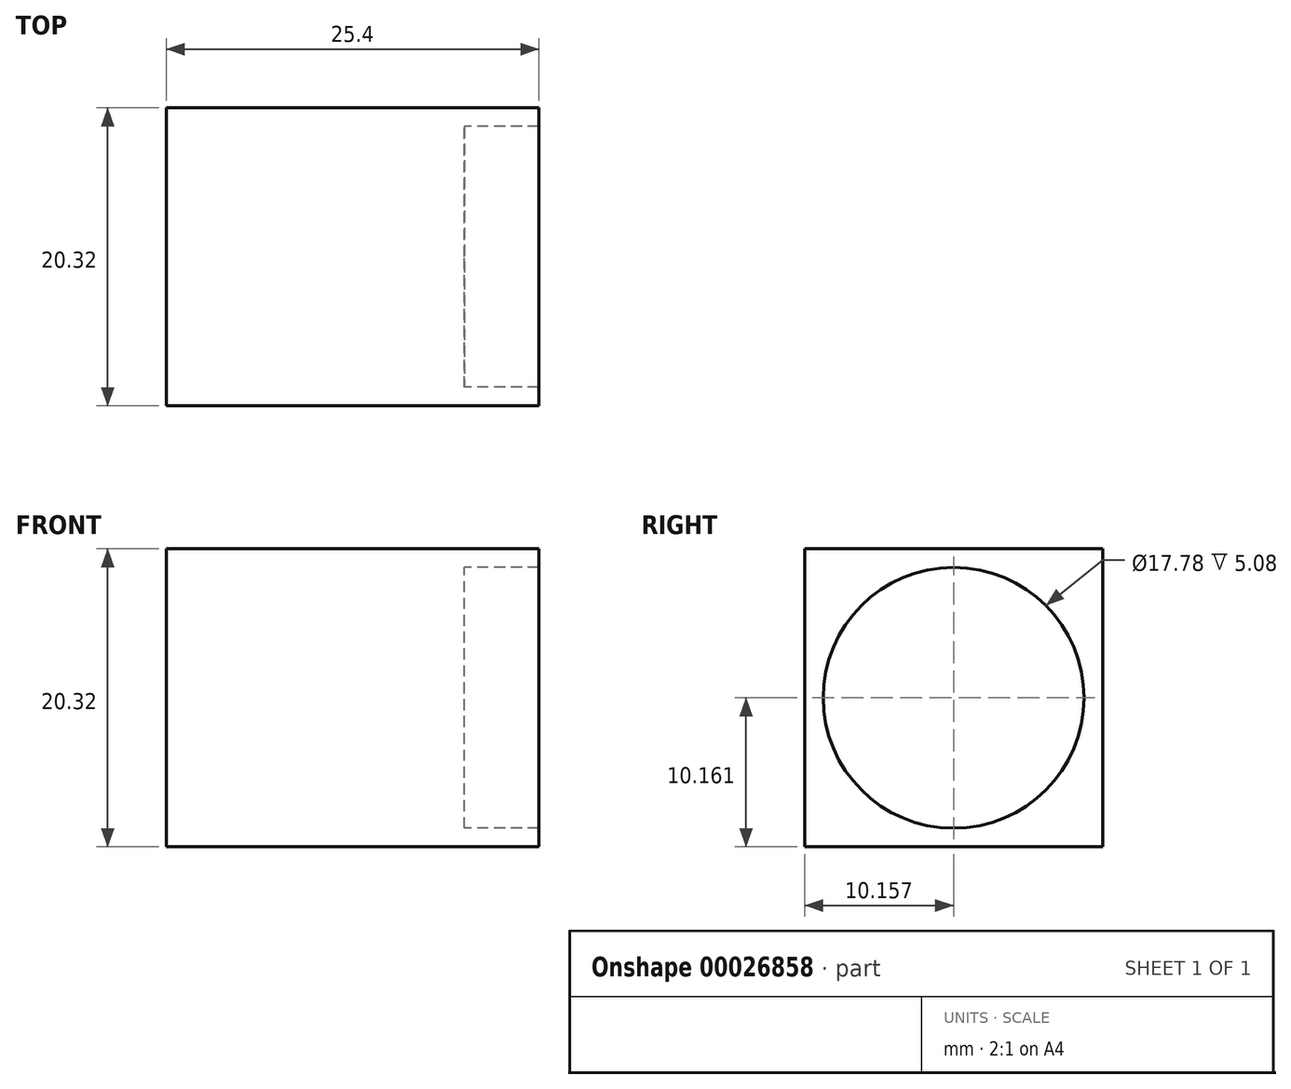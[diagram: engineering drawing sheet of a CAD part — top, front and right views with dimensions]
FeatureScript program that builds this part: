
annotation { "Feature Type Name" : "Feature", "Feature Type Description" : "" }
export const myFeature = defineFeature(function(context is Context, id is Id, definition is map)
    precondition{}
    {
        {
            var Q0;
            Q0=qCreatedBy(makeId("Right.planeOp"),FACE);
            var sketch = newSketch(context, id + "F0", { "sketchPlane" : qUnion([Q0])});
            skLineSegment(sketch, "E0.bottom", {"start": v(-57.34, 11.07) * mm, "end": v(-37.02, 11.07) * mm});
            skLineSegment(sketch, "E0.top", {"start": v(-57.34, -9.25) * mm, "end": v(-37.02, -9.25) * mm});
            skLineSegment(sketch, "E0.left", {"start": v(-57.34, 11.07) * mm, "end": v(-57.34, -9.25) * mm});
            skLineSegment(sketch, "E0.right", {"start": v(-37.02, 11.07) * mm, "end": v(-37.02, -9.25) * mm});
            skCircle(sketch, "E1", {"center": v(-47.18, 0.91) * mm, "radius": 8.9 * mm});
            skPoint(sketch, "E2.orphan", {"position": v(-57.34, 0.91) * mm});
            skPoint(sketch, "E3.end.orphan", {"position": v(-37.02, 0.91) * mm});
            skPoint(sketch, "E4.start.orphan", {"position": v(-47.18, 11.07) * mm});
            skPoint(sketch, "E5.trimOffspring.end.orphan", {"position": v(-47.18, -9.25) * mm});
            skSolve(sketch);
        }
        {
            var Q0;
            Q0=makeQuery(id+"F0.imprint","IMPRINT",FACE,{"disambiguationData":[TD([[makeQuery(id+"F0.imprint","IMPRINT",EDGE,{"derivedFrom":sQuery(id+"F0.wireOp",EDGE,"E0.bottom")}),-1.0]])]});
            extrude(context, id + "F1", {"entities" : qUnion([Q0]), "depth" : 25.4 * mm});
        }
        {
            var Q0;
            Q0=makeQuery(id+"F0.imprint","IMPRINT",FACE,{"disambiguationData":[TD([[makeQuery(id+"F0.imprint","IMPRINT",EDGE,{"derivedFrom":sQuery(id+"F0.wireOp",EDGE,"E1")}),1.0]])]});
            extrude(context, id + "F2", {"entities" : qUnion([Q0]), "operationType" : NewBodyOperationType.ADD, "depth" : 20.32 * mm});
        }
    });
